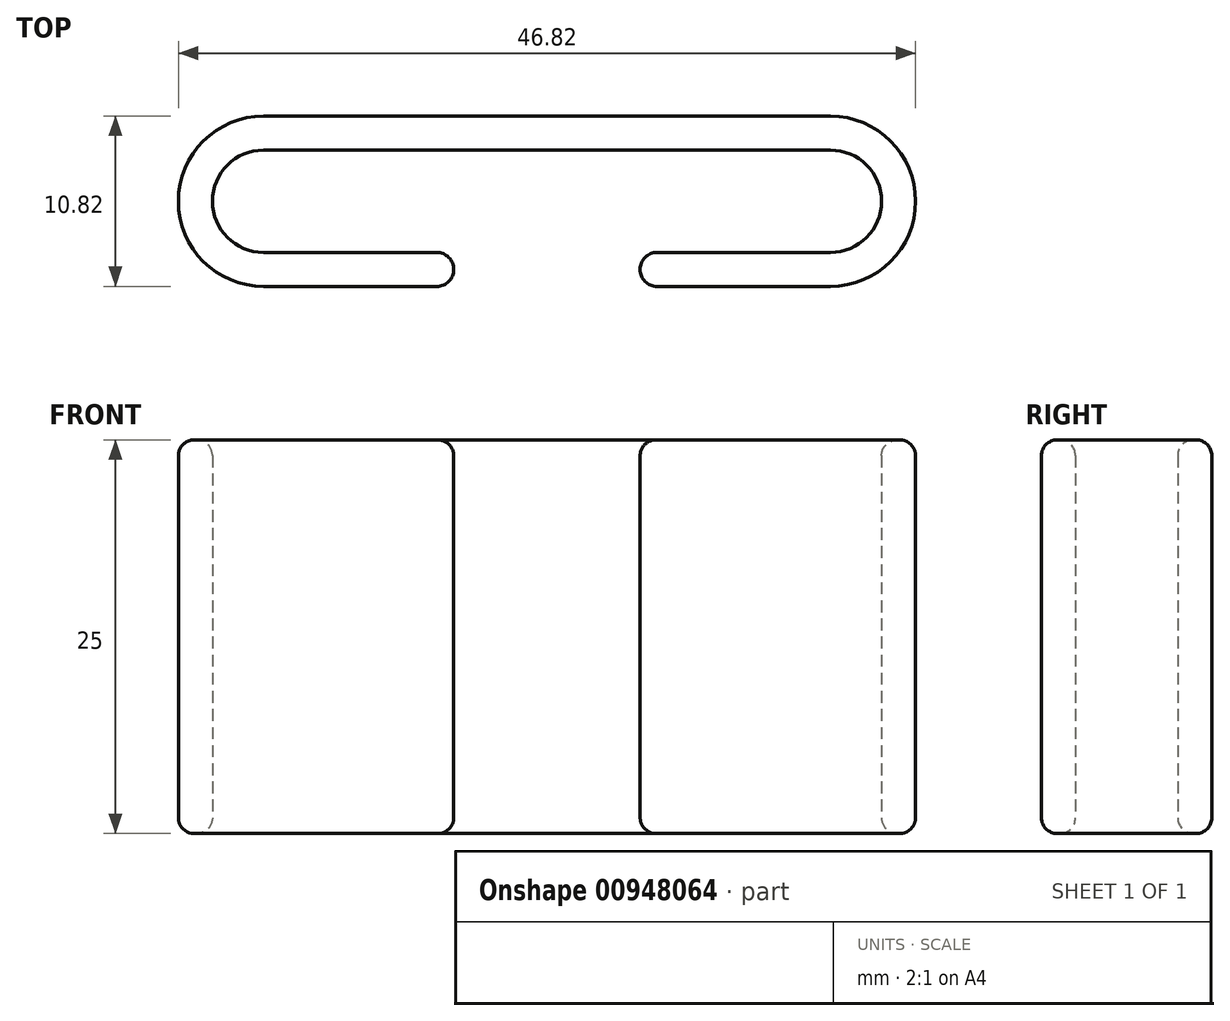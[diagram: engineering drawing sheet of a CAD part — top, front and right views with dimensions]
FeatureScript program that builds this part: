
annotation { "Feature Type Name" : "Feature", "Feature Type Description" : "" }
export const myFeature = defineFeature(function(context is Context, id is Id, definition is map)
    precondition{}
    {
        {
            var Q0;
            Q0=qCreatedBy(makeId("Top.planeOp"),FACE);
            var sketch = newSketch(context, id + "F0", { "sketchPlane" : qUnion([Q0])});
            skLineSegment(sketch, "E0", {"start": v(-18, 15.69) * mm, "end": v(18, 15.69) * mm});
            skLineSegment(sketch, "E1", {"start": v(-18, 17.85) * mm, "end": v(18, 17.85) * mm});
            skLineSegment(sketch, "E2", {"start": v(-7, 9.19) * mm, "end": v(-18, 9.19) * mm});
            skLineSegment(sketch, "E3", {"start": v(-7, 7.03) * mm, "end": v(-18, 7.03) * mm});
            skLineSegment(sketch, "E4", {"start": v(7, 9.19) * mm, "end": v(18, 9.19) * mm});
            skLineSegment(sketch, "E5", {"start": v(7, 7.03) * mm, "end": v(18, 7.03) * mm});
            skArc(sketch, "E6", {"start": v(-18, 17.85) * mm, "mid": v(-23.41, 12.44) * mm, "end": v(-18, 7.03) * mm});
            skArc(sketch, "E7", {"start": v(-18, 15.69) * mm, "mid": v(-21.25, 12.44) * mm, "end": v(-18, 9.19) * mm});
            skArc(sketch, "E8", {"start": v(18, 7.03) * mm, "mid": v(23.4, 12.44) * mm, "end": v(18, 17.85) * mm});
            skArc(sketch, "E9", {"start": v(18, 9.19) * mm, "mid": v(21.25, 12.44) * mm, "end": v(18, 15.69) * mm});
            skArc(sketch, "E10", {"start": v(-7, 7.03) * mm, "mid": v(-5.92, 8.1) * mm, "end": v(-7, 9.19) * mm});
            skArc(sketch, "E11", {"start": v(7, 9.19) * mm, "mid": v(5.92, 8.1) * mm, "end": v(7, 7.03) * mm});
            skSolve(sketch);
        }
        {
            var Q0;
            Q0=makeQuery(id+"F0.imprint","IMPRINT",FACE,{"disambiguationData":[TD([[makeQuery(id+"F0.imprint","IMPRINT",EDGE,{"derivedFrom":sQuery(id+"F0.wireOp",EDGE,"E0")}),1.0]])]});
            extrude(context, id + "F1", {"entities" : qUnion([Q0]), "depth" : 25 * mm, "offsetDistance" : 25 * mm});
        }
        {
            var Q0;
            Q0=makeQuery(id+"F1.opExtrude","CAP_EDGE",EDGE,{"disambiguationData":[OSD([sQuery(id+"F0.wireOp",EDGE,"E1")])],"isStart":false});
            var Q1;
            Q1=makeQuery(id+"F1.opExtrude","CAP_EDGE",EDGE,{"disambiguationData":[OSD([sQuery(id+"F0.wireOp",EDGE,"E0")])],"isStart":false});
            var Q2;
            Q2=makeQuery(id+"F1.opExtrude","CAP_EDGE",EDGE,{"disambiguationData":[OSD([sQuery(id+"F0.wireOp",EDGE,"E9")])],"isStart":false});
            var Q3;
            Q3=makeQuery(id+"F1.opExtrude","CAP_EDGE",EDGE,{"disambiguationData":[OSD([sQuery(id+"F0.wireOp",EDGE,"E8")])],"isStart":false});
            var Q4;
            Q4=makeQuery(id+"F1.opExtrude","CAP_EDGE",EDGE,{"disambiguationData":[OSD([sQuery(id+"F0.wireOp",EDGE,"E4")])],"isStart":false});
            var Q5;
            Q5=makeQuery(id+"F1.opExtrude","CAP_EDGE",EDGE,{"disambiguationData":[OSD([sQuery(id+"F0.wireOp",EDGE,"E5")])],"isStart":false});
            var Q6;
            Q6=makeQuery(id+"F1.opExtrude","CAP_EDGE",EDGE,{"disambiguationData":[OSD([sQuery(id+"F0.wireOp",EDGE,"E11")])],"isStart":false});
            var Q7;
            Q7=makeQuery(id+"F1.opExtrude","CAP_EDGE",EDGE,{"disambiguationData":[OSD([sQuery(id+"F0.wireOp",EDGE,"E10")])],"isStart":false});
            var Q8;
            Q8=makeQuery(id+"F1.opExtrude","CAP_EDGE",EDGE,{"disambiguationData":[OSD([sQuery(id+"F0.wireOp",EDGE,"E7")])],"isStart":false});
            var Q9;
            Q9=makeQuery(id+"F1.opExtrude","CAP_EDGE",EDGE,{"disambiguationData":[OSD([sQuery(id+"F0.wireOp",EDGE,"E2")])],"isStart":false});
            var Q10;
            Q10=makeQuery(id+"F1.opExtrude","CAP_EDGE",EDGE,{"disambiguationData":[OSD([sQuery(id+"F0.wireOp",EDGE,"E3")])],"isStart":false});
            var Q11;
            Q11=makeQuery(id+"F1.opExtrude","CAP_EDGE",EDGE,{"disambiguationData":[OSD([sQuery(id+"F0.wireOp",EDGE,"E6")])],"isStart":false});
            var Q12;
            Q12=makeQuery(id+"F1.opExtrude","CAP_EDGE",EDGE,{"disambiguationData":[OSD([sQuery(id+"F0.wireOp",EDGE,"E5")])],"isStart":true});
            var Q13;
            Q13=makeQuery(id+"F1.opExtrude","CAP_EDGE",EDGE,{"disambiguationData":[OSD([sQuery(id+"F0.wireOp",EDGE,"E8")])],"isStart":true});
            var Q14;
            Q14=makeQuery(id+"F1.opExtrude","CAP_EDGE",EDGE,{"disambiguationData":[OSD([sQuery(id+"F0.wireOp",EDGE,"E1")])],"isStart":true});
            var Q15;
            Q15=makeQuery(id+"F1.opExtrude","CAP_EDGE",EDGE,{"disambiguationData":[OSD([sQuery(id+"F0.wireOp",EDGE,"E0")])],"isStart":true});
            var Q16;
            Q16=makeQuery(id+"F1.opExtrude","CAP_EDGE",EDGE,{"disambiguationData":[OSD([sQuery(id+"F0.wireOp",EDGE,"E9")])],"isStart":true});
            var Q17;
            Q17=makeQuery(id+"F1.opExtrude","CAP_EDGE",EDGE,{"disambiguationData":[OSD([sQuery(id+"F0.wireOp",EDGE,"E2")])],"isStart":true});
            var Q18;
            Q18=makeQuery(id+"F1.opExtrude","CAP_EDGE",EDGE,{"disambiguationData":[OSD([sQuery(id+"F0.wireOp",EDGE,"E10")])],"isStart":true});
            var Q19;
            Q19=makeQuery(id+"F1.opExtrude","CAP_EDGE",EDGE,{"disambiguationData":[OSD([sQuery(id+"F0.wireOp",EDGE,"E11")])],"isStart":true});
            var Q20;
            Q20=makeQuery(id+"F1.opExtrude","CAP_EDGE",EDGE,{"disambiguationData":[OSD([sQuery(id+"F0.wireOp",EDGE,"E4")])],"isStart":true});
            var Q21;
            Q21=makeQuery(id+"F1.opExtrude","CAP_EDGE",EDGE,{"disambiguationData":[OSD([sQuery(id+"F0.wireOp",EDGE,"E6")])],"isStart":true});
            var Q22;
            Q22=makeQuery(id+"F1.opExtrude","CAP_EDGE",EDGE,{"disambiguationData":[OSD([sQuery(id+"F0.wireOp",EDGE,"E7")])],"isStart":true});
            fillet(context, id + "F2", {"entities" : qUnion([Q0, Q1, Q2, Q3, Q4, Q5, Q6, Q7, Q8, Q9, Q10, Q11, Q12, Q13, Q14, Q15, Q16, Q17, Q18, Q19, Q20, Q21, Q22]), "radius" : 1 * mm, "tangentPropagation" : true, "allowEdgeOverflow" : false});
        }
    });
